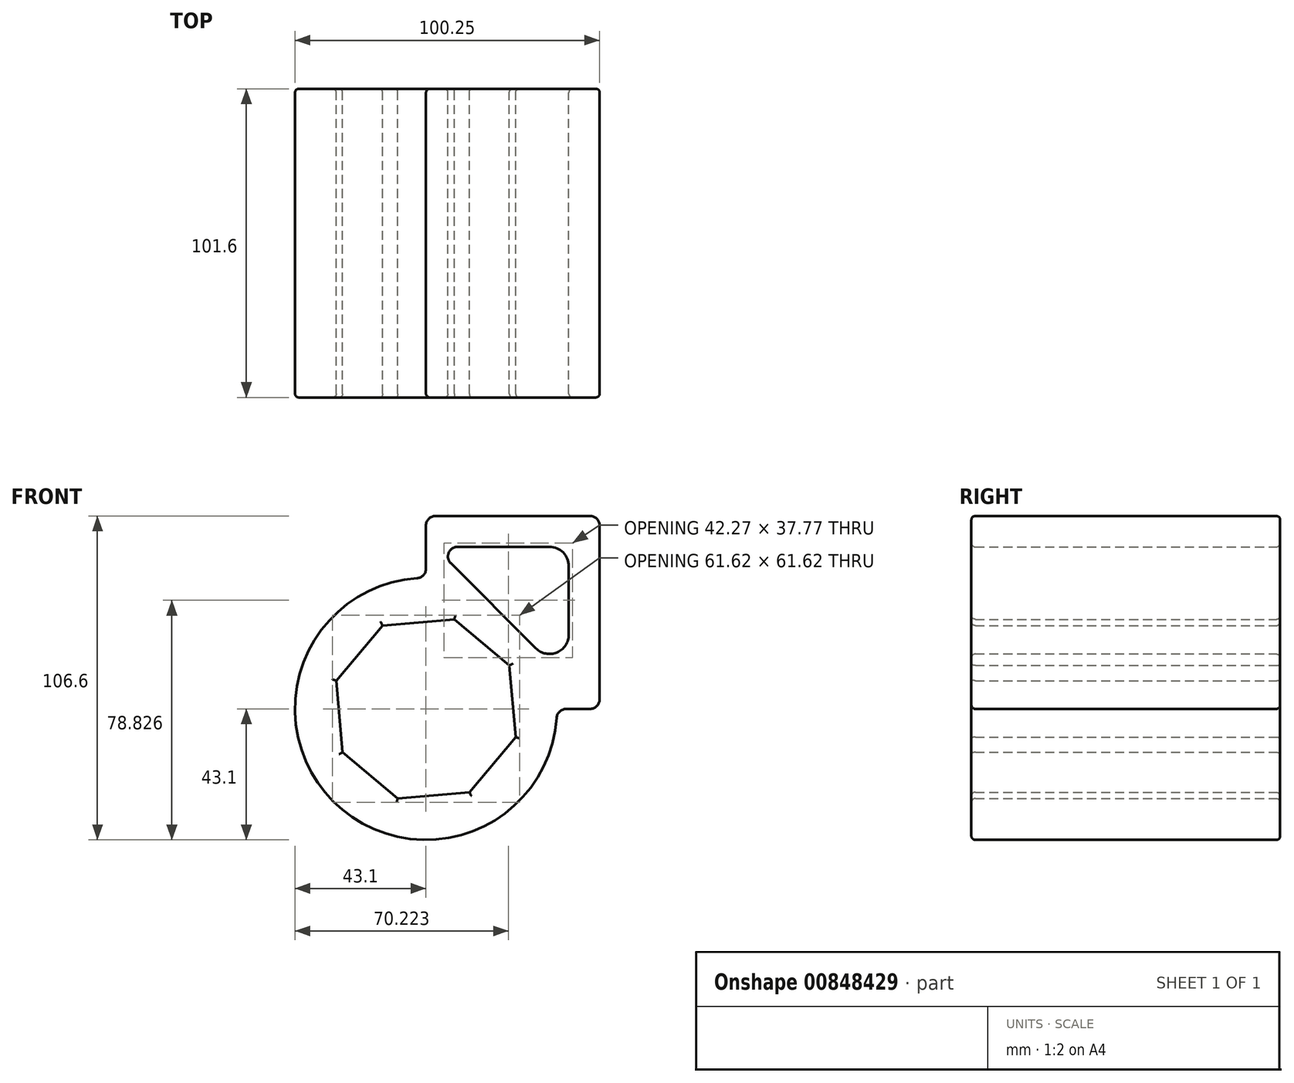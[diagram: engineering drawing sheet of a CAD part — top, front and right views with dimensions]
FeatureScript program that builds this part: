
annotation { "Feature Type Name" : "Feature", "Feature Type Description" : "" }
export const myFeature = defineFeature(function(context is Context, id is Id, definition is map)
    precondition{}
    {
        {
            var Q0;
            Q0=qCreatedBy(makeId("Front.planeOp"),FACE);
            var sketch = newSketch(context, id + "F0", { "sketchPlane" : qUnion([Q0])});
            skLineSegment(sketch, "E0", {"start": v(0, 46.17) * mm, "end": v(0, 60.32) * mm});
            skLineSegment(sketch, "E1", {"start": v(3.17, 63.5) * mm, "end": v(53.98, 63.5) * mm});
            skLineSegment(sketch, "E2", {"start": v(57.15, 60.32) * mm, "end": v(57.15, 3.18) * mm});
            skLineSegment(sketch, "E3", {"start": v(53.98, 0) * mm, "end": v(46.17, 0) * mm});
            skArc(sketch, "E4", {"start": v(-2.96, 43) * mm, "mid": v(-30.48, -30.48) * mm, "end": v(43, -2.96) * mm});
            skCircle(sketch, "E5.cCircle", {"center": v(0, 0) * mm, "radius": 28.57 * mm, "construction": true});
            skLineSegment(sketch, "E5.0", {"start": v(9.3, 29.5) * mm, "end": v(27.43, 14.28) * mm});
            skLineSegment(sketch, "E5.1", {"start": v(27.43, 14.28) * mm, "end": v(29.5, -9.3) * mm});
            skLineSegment(sketch, "E5.2", {"start": v(29.5, -9.3) * mm, "end": v(14.28, -27.43) * mm});
            skLineSegment(sketch, "E5.3", {"start": v(14.28, -27.43) * mm, "end": v(-9.3, -29.5) * mm});
            skLineSegment(sketch, "E5.4", {"start": v(-9.3, -29.5) * mm, "end": v(-27.43, -14.28) * mm});
            skLineSegment(sketch, "E5.5", {"start": v(-27.43, -14.28) * mm, "end": v(-29.5, 9.3) * mm});
            skLineSegment(sketch, "E5.6", {"start": v(-29.5, 9.3) * mm, "end": v(-14.28, 27.43) * mm});
            skLineSegment(sketch, "E5.7", {"start": v(-14.28, 27.43) * mm, "end": v(9.3, 29.5) * mm});
            skPoint(sketch, "E5.0.midPoint", {"position": v(18.37, 21.89) * mm});
            skPoint(sketch, "E6.visualSharp", {"position": v(57.15, 0) * mm});
            skArc(sketch, "E6.filletArc", {"start": v(53.98, 0) * mm, "mid": v(56.22, 0.93) * mm, "end": v(57.15, 3.18) * mm});
            skPoint(sketch, "E7.visualSharp", {"position": v(57.15, 63.5) * mm});
            skArc(sketch, "E7.filletArc", {"start": v(57.15, 60.32) * mm, "mid": v(56.22, 62.57) * mm, "end": v(53.98, 63.5) * mm});
            skPoint(sketch, "E8.visualSharp", {"position": v(0, 63.5) * mm});
            skArc(sketch, "E8.filletArc", {"start": v(3.17, 63.5) * mm, "mid": v(0.93, 62.57) * mm, "end": v(0, 60.32) * mm});
            skPoint(sketch, "E9.visualSharp", {"position": v(0, 43.1) * mm});
            skArc(sketch, "E9.filletArc", {"start": v(-2.96, 43) * mm, "mid": v(-0.85, 44) * mm, "end": v(0, 46.17) * mm});
            skPoint(sketch, "E10.visualSharp", {"position": v(43.1, 0) * mm});
            skArc(sketch, "E10.filletArc", {"start": v(46.17, 0) * mm, "mid": v(44, -0.85) * mm, "end": v(43, -2.96) * mm});
            skLineSegment(sketch, "E11", {"start": v(10.4, 53.34) * mm, "end": v(40.64, 53.34) * mm});
            skLineSegment(sketch, "E12", {"start": v(47, 46.99) * mm, "end": v(47, 24.42) * mm});
            skLineSegment(sketch, "E13", {"start": v(36.15, 19.93) * mm, "end": v(8.16, 47.92) * mm});
            skPoint(sketch, "E14.visualSharp", {"position": v(2.74, 53.34) * mm});
            skArc(sketch, "E14.filletArc", {"start": v(10.4, 53.34) * mm, "mid": v(7.48, 51.38) * mm, "end": v(8.16, 47.92) * mm});
            skPoint(sketch, "E15.visualSharp", {"position": v(47, 9.1) * mm});
            skArc(sketch, "E15.filletArc", {"start": v(36.15, 19.93) * mm, "mid": v(43.07, 18.56) * mm, "end": v(47, 24.42) * mm});
            skPoint(sketch, "E16.visualSharp", {"position": v(47, 53.34) * mm});
            skArc(sketch, "E16.filletArc", {"start": v(47, 46.99) * mm, "mid": v(45.13, 51.48) * mm, "end": v(40.64, 53.34) * mm});
            skSolve(sketch);
        }
        {
            var Q0;
            Q0 = qSketchRegion(id + "F0", true);
            extrude(context, id + "F1", {"entities" : qUnion([Q0]), "depth" : 101.6 * mm, "offsetDistance" : 25.4 * mm, "symmetric" : true});
        }
        {
            var Q0;
            Q0=makeQuery(id+"F1.opExtrude","CAP_FACE",FACE,{"disambiguationData":[OSD([sQuery(id+"F0.wireOp",EDGE,"E0"),sQuery(id+"F0.wireOp",EDGE,"E1"),sQuery(id+"F0.wireOp",EDGE,"E2"),sQuery(id+"F0.wireOp",EDGE,"E3"),sQuery(id+"F0.wireOp",EDGE,"E4"),sQuery(id+"F0.wireOp",EDGE,"E5.0"),sQuery(id+"F0.wireOp",EDGE,"E5.1"),sQuery(id+"F0.wireOp",EDGE,"E5.2"),sQuery(id+"F0.wireOp",EDGE,"E5.3"),sQuery(id+"F0.wireOp",EDGE,"E5.4"),sQuery(id+"F0.wireOp",EDGE,"E5.5"),sQuery(id+"F0.wireOp",EDGE,"E5.6"),sQuery(id+"F0.wireOp",EDGE,"E5.7"),sQuery(id+"F0.wireOp",EDGE,"E6.filletArc"),sQuery(id+"F0.wireOp",EDGE,"E7.filletArc"),sQuery(id+"F0.wireOp",EDGE,"E8.filletArc"),sQuery(id+"F0.wireOp",EDGE,"E9.filletArc"),sQuery(id+"F0.wireOp",EDGE,"E10.filletArc"),sQuery(id+"F0.wireOp",EDGE,"E11"),sQuery(id+"F0.wireOp",EDGE,"E12"),sQuery(id+"F0.wireOp",EDGE,"E13"),sQuery(id+"F0.wireOp",EDGE,"E14.filletArc"),sQuery(id+"F0.wireOp",EDGE,"E15.filletArc"),sQuery(id+"F0.wireOp",EDGE,"E16.filletArc")])],"isStart":false});
            var Q1;
            Q1=makeQuery(id+"F1.opExtrude","CAP_FACE",FACE,{"disambiguationData":[OSD([sQuery(id+"F0.wireOp",EDGE,"E0"),sQuery(id+"F0.wireOp",EDGE,"E1"),sQuery(id+"F0.wireOp",EDGE,"E2"),sQuery(id+"F0.wireOp",EDGE,"E3"),sQuery(id+"F0.wireOp",EDGE,"E4"),sQuery(id+"F0.wireOp",EDGE,"E5.0"),sQuery(id+"F0.wireOp",EDGE,"E5.1"),sQuery(id+"F0.wireOp",EDGE,"E5.2"),sQuery(id+"F0.wireOp",EDGE,"E5.3"),sQuery(id+"F0.wireOp",EDGE,"E5.4"),sQuery(id+"F0.wireOp",EDGE,"E5.5"),sQuery(id+"F0.wireOp",EDGE,"E5.6"),sQuery(id+"F0.wireOp",EDGE,"E5.7"),sQuery(id+"F0.wireOp",EDGE,"E6.filletArc"),sQuery(id+"F0.wireOp",EDGE,"E7.filletArc"),sQuery(id+"F0.wireOp",EDGE,"E8.filletArc"),sQuery(id+"F0.wireOp",EDGE,"E9.filletArc"),sQuery(id+"F0.wireOp",EDGE,"E10.filletArc"),sQuery(id+"F0.wireOp",EDGE,"E11"),sQuery(id+"F0.wireOp",EDGE,"E12"),sQuery(id+"F0.wireOp",EDGE,"E13"),sQuery(id+"F0.wireOp",EDGE,"E14.filletArc"),sQuery(id+"F0.wireOp",EDGE,"E15.filletArc"),sQuery(id+"F0.wireOp",EDGE,"E16.filletArc")])],"isStart":true});
            fillet(context, id + "F2", {"entities" : qUnion([Q0, Q1]), "radius" : 1.27 * mm, "tangentPropagation" : true, "allowEdgeOverflow" : false});
        }
    });
